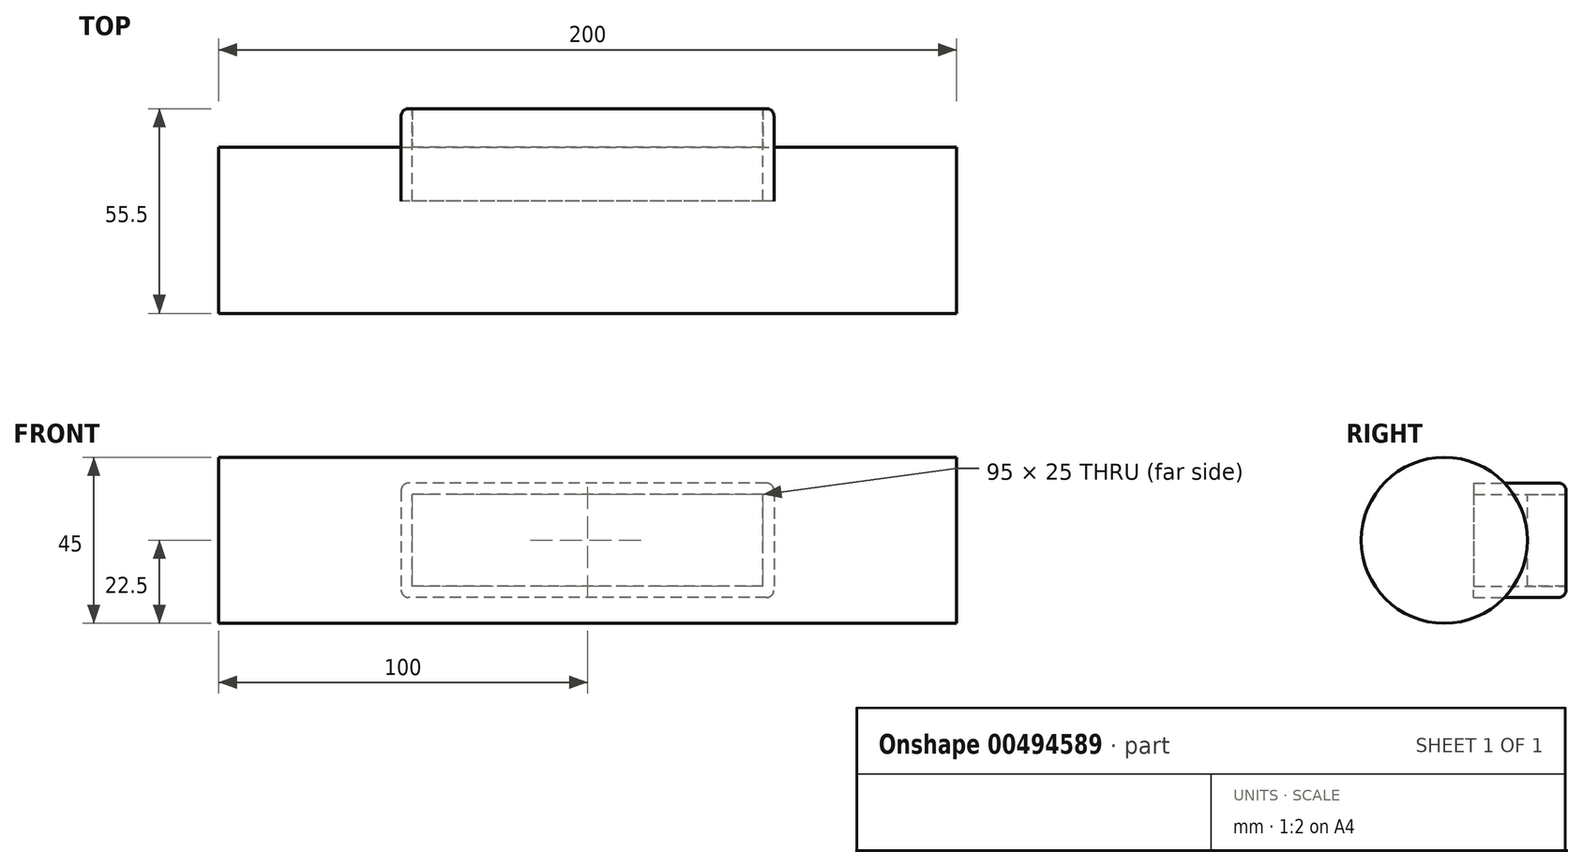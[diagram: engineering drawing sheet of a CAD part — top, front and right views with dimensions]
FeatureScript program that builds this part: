
annotation { "Feature Type Name" : "Feature", "Feature Type Description" : "" }
export const myFeature = defineFeature(function(context is Context, id is Id, definition is map)
    precondition{}
    {
        {
            var Q0;
            Q0=qCreatedBy(makeId("Right.planeOp"),FACE);
            var sketch = newSketch(context, id + "F0", { "sketchPlane" : qUnion([Q0])});
            skCircle(sketch, "E0", {"center": v(-22.5, 0) * mm, "radius": 22.5 * mm});
            skLineSegment(sketch, "E1", {"start": v(0, 0) * mm, "end": v(0, 12.5) * mm});
            skLineSegment(sketch, "E2", {"start": v(0, 12.5) * mm, "end": v(10.5, 12.5) * mm});
            skLineSegment(sketch, "E3", {"start": v(10.5, 12.5) * mm, "end": v(10.5, -12.5) * mm});
            skLineSegment(sketch, "E4", {"start": v(10.5, -12.5) * mm, "end": v(0, -12.5) * mm});
            skLineSegment(sketch, "E5", {"start": v(0, -12.5) * mm, "end": v(0, 0) * mm});
            skSolve(sketch);
        }
        {
            var Q0;
            {var subQ0=sQuery(id+"F0.wireOp",EDGE,"E0");var subQ2=makeQuery(id+"F0.imprint","INTERSECT",VERTEX,{"derivedFrom":[subQ0,sQuery(id+"F0.wireOp",EDGE,"sMKVGwX0-ooi8-n9OW-R0VL-jmy8f2mgR9Dp")]});Q0=makeQuery(id+"F0.imprint","IMPRINT",FACE,{"disambiguationData":[TD([[makeQuery(id+"F0.imprint","IMPRINT",EDGE,{"disambiguationData":[TD([[subQ2,1.0]])],"derivedFrom":subQ0}),1.0]])]});}
            extrude(context, id + "F1", {"entities" : qUnion([Q0]), "oppositeDirection" : true, "depth" : 200 * mm, "offsetDistance" : 25 * mm, "symmetric" : true});
        }
        {
            var Q0;
            Q0=makeQuery(id+"F0.imprint","IMPRINT",FACE,{"disambiguationData":[TD([[makeQuery(id+"F0.imprint","IMPRINT",EDGE,{"derivedFrom":sQuery(id+"F0.wireOp",EDGE,"E1")}),-1.0]])]});
            extrude(context, id + "F2", {"entities" : qUnion([Q0]), "operationType" : NewBodyOperationType.ADD, "depth" : 95 * mm, "offsetDistance" : 25 * mm, "symmetric" : true});
        }
        {
            var Q0;
            Q0=makeQuery(id+"F2.opExtrude","SWEPT_FACE",FACE,{"disambiguationData":[OSD([sQuery(id+"F0.wireOp",EDGE,"E3")])]});
            var sketch = newSketch(context, id + "F3", { "sketchPlane" : qUnion([Q0])});
            skLineSegment(sketch, "E6.bottom", {"start": v(-50.5, 15.5) * mm, "end": v(50.5, 15.5) * mm});
            skLineSegment(sketch, "E6.top", {"start": v(-50.5, -15.5) * mm, "end": v(50.5, -15.5) * mm});
            skLineSegment(sketch, "E6.left", {"start": v(-50.5, 15.5) * mm, "end": v(-50.5, -15.5) * mm});
            skLineSegment(sketch, "E6.right", {"start": v(50.5, 15.5) * mm, "end": v(50.5, -15.5) * mm});
            skLineSegment(sketch, "E7.0", {"start": v(-47.5, 12.5) * mm, "end": v(47.5, 12.5) * mm});
            skLineSegment(sketch, "E8.0", {"start": v(-47.5, 12.5) * mm, "end": v(-47.5, -12.5) * mm});
            skLineSegment(sketch, "E9.0", {"start": v(-47.5, -12.5) * mm, "end": v(47.5, -12.5) * mm});
            skLineSegment(sketch, "E10.0.0", {"start": v(47.5, -12.5) * mm, "end": v(47.5, 12.5) * mm});
            skLineSegment(sketch, "E10.0.1", {"start": v(47.5, 12.5) * mm, "end": v(-47.5, 12.5) * mm});
            skSolve(sketch);
        }
        {
            var Q0;
            Q0=makeQuery(id+"F3.imprint","IMPRINT",FACE,{"disambiguationData":[TD([[makeQuery(id+"F3.imprint","IMPRINT",EDGE,{"derivedFrom":sQuery(id+"F3.wireOp",EDGE,"E6.bottom")}),-1.0]])]});
            extrude(context, id + "F4", {"entities" : qUnion([Q0]), "oppositeDirection" : true, "depth" : 25 * mm, "offsetDistance" : 25 * mm});
        }
        {
            var Q0;
            Q0=makeQuery(id+"F4.opExtrude","SWEPT_EDGE",EDGE,{"disambiguationData":[OSD([sQuery(id+"F3.wireOp",EDGE,"E6.bottom"),sQuery(id+"F3.wireOp",EDGE,"E6.left")])]});
            var Q1;
            Q1=makeQuery(id+"F4.opExtrude","SWEPT_EDGE",EDGE,{"disambiguationData":[OSD([sQuery(id+"F3.wireOp",EDGE,"E6.top"),sQuery(id+"F3.wireOp",EDGE,"E6.left")])]});
            var Q2;
            Q2=makeQuery(id+"F4.opExtrude","SWEPT_EDGE",EDGE,{"disambiguationData":[OSD([sQuery(id+"F3.wireOp",EDGE,"E6.bottom"),sQuery(id+"F3.wireOp",EDGE,"E6.right")])]});
            var Q3;
            Q3=makeQuery(id+"F4.opExtrude","SWEPT_EDGE",EDGE,{"disambiguationData":[OSD([sQuery(id+"F3.wireOp",EDGE,"E6.top"),sQuery(id+"F3.wireOp",EDGE,"E6.right")])]});
            var Q4;
            Q4=makeQuery(id+"F4.opExtrude","CAP_EDGE",EDGE,{"disambiguationData":[OSD([sQuery(id+"F3.wireOp",EDGE,"E6.bottom")])],"isStart":true});
            var Q5;
            Q5=makeQuery(id+"F4.opExtrude","CAP_EDGE",EDGE,{"disambiguationData":[OSD([sQuery(id+"F3.wireOp",EDGE,"E6.left")])],"isStart":true});
            var Q6;
            Q6=makeQuery(id+"F4.opExtrude","CAP_EDGE",EDGE,{"disambiguationData":[OSD([sQuery(id+"F3.wireOp",EDGE,"E6.top")])],"isStart":true});
            var Q7;
            Q7=makeQuery(id+"F4.opExtrude","CAP_EDGE",EDGE,{"disambiguationData":[OSD([sQuery(id+"F3.wireOp",EDGE,"E6.right")])],"isStart":true});
            fillet(context, id + "F5", {"entities" : qUnion([Q0, Q1, Q2, Q3, Q4, Q5, Q6, Q7]), "radius" : 2 * mm, "tangentPropagation" : true, "allowEdgeOverflow" : false});
        }
    });
